# Revit family: MI-950 -F
name_source: partatom
category: Plumbing Fixtures
revit_build: Autodesk Revit 2013 (Build: 20120221_2030(x64)
units: mm (PartAtom-declared; Revit-internal decimal feet)

## types (3) — shared parameters
Body Material = Cast Iron
Description = Deep seal trap with funnel
Manufacturer = Mifab
Model = MI-950-F
URL = www.mifab.com
material = Bronze

## per-type parameters (varying)
| type | A | B | C | C1 | D | D12 | E | Hright of Plug | PLug 2 | Plug 1' | Plug 11 | Plug1 | Thickness of A | d1 | d2 |
| MI-952-F | 1' - 0" | 10' - 6" | 5' - 0" | 4' - 3" | 6' - 6" | 2' - 0 3/16" | 2' - 9" | 0' - 5 13/32" | 1' - 7 3/16" | 0' - 10" | 1' - 6 3/16" | 1' - 3 19/32" | 1' - 2 13/32" | 4' - 2 11/16" | 4' - 4" |
| MI-953-F | 1' - 6" | 13' - 6" | 5' - 3" | 4' - 5 9/16" | 8' - 0" | 2' - 5 3/4" | 3' - 6" | 0' - 5 21/32" | 2' - 4 13/16" | 1' - 3" | 1' - 10 13/32" | 1' - 7 3/16" | 1' - 9 19/32" | 5' - 2 13/32" | 5' - 4" |
| MI-954-F | 2' - 0" | 15' - 3" | 6' - 9" | 5' - 8 27/32" | 10' - 0" | 3' - 1 3/16" | 4' - 3" | 0' - 7 9/32" | 3' - 2 13/32" | 1' - 8" | 2' - 4" | 2' - 0" | 2' - 4 13/16" | 6' - 6" | 6' - 8" |

## geometry (parser evidence)
native form markers: Blend x4, Sweep x1
no freeform markers — native parametric forms only
